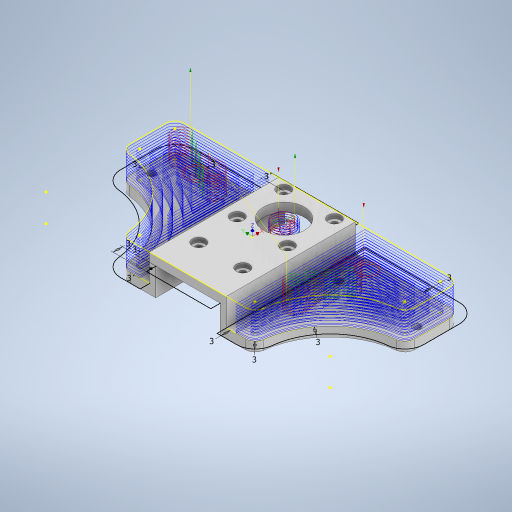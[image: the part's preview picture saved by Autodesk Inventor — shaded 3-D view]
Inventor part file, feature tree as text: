
AUTODESK INVENTOR PART (.ipt)
format: ipt  version: 2024.2 (Build 282272000, 272)  size: 674,816 bytes
history: native  units: in
note: dims shown in document units (in); Inventor stores cm internally (conversion verified against a paired STEP export)
features: sketch x8, projected_geometry x3, extrude x1, mirror x1, fillet x1, plane x1
ambient origin geometry x8: Origin, YZ Plane, XZ Plane, XY Plane, X Axis, Y Axis, Z Axis, Center Point
bodies: Solid1 (feature_tree)
feature tree (15):
  extrude  "Extrusion1"  Depth=0.1122in
  mirror  "Mirror1"
  fillet  "Fillet3"  Radius=0.2283in
  sketch  "Sketch15"  dims[d11=1.6181in d12=0.0in]
  sketch  "Sketch16"  dims[d42=0.1181in]
  sketch  "Sketch17"  dims[d43=0.9843in d44=0.0996in d45=0.2362in d46=0.1575in d47=0.0787in d48=90.0deg d49=0.315in d50=0.8108in d51=0.4114in d53=0.1181in d60=0.9449in d61=0.3937in d62=0.0in d73=1.2992in d74=1.2992in d75=0.5118in d76=0.4133in d77=0.3937in d78=0.0in d86=0.0827in d87=0.2362in d88=0.1614in d89=0.0551in d90=90.0deg d91=0.315in d92=0.8108in d125=0.1181in d126=0.1181in d127=0.1181in d136=0.1181in d137=0.1181in d138=0.1181in d139=0.1181in d140=0.1181in d141=0.1181in d142=0.1181in d143=0.1181in d63=0.0059in d64=0.0098in d65=0.0148in d66=0.5635in d67=0.0295in d68=0.8108in d69=0.0025in d70=0.0295in d71=0.0148in]
  sketch  "Sketch1"  dims[d0=0.8067in d1=0.1122in d3=0.2283in]
  sketch  "Sketch8"  dims[d4=0.1181in]
  projected_geometry  "Projected Loop3"
  sketch  "Sketch9"  dims[d5=0.1181in]
  projected_geometry  "Projected Loop5"
  plane  "Work Plane1"
  sketch  "Sketch10"  dims[d6=1.378in]
  projected_geometry  "Projected Loop6"
  sketch  "Sketch11"  dims[d7=1.378in]
